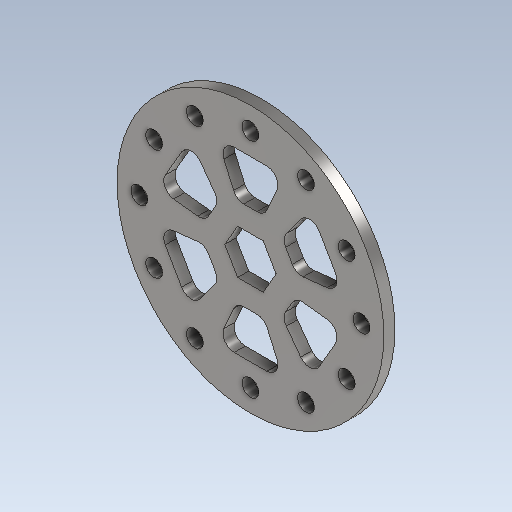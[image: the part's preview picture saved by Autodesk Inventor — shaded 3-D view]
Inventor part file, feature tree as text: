
AUTODESK INVENTOR PART (.ipt)
format: ipt  version: 2023 (Build 270158000, 158)  size: 222,208 bytes
history: native  units: in
note: dims shown in document units (in); Inventor stores cm internally (conversion verified against a paired STEP export)
features: extrude x2, sketch x1, fillet x1, pattern_circular x1
ambient origin geometry x8: Origin, YZ Plane, XZ Plane, XY Plane, X Axis, Y Axis, Z Axis, Center Point
bodies: Solid1 (feature_tree)
feature tree (5):
  sketch  "Sketch1"  dims[d0=3.0in d1=0.5in d2=2.5in d3=0.19in d4=4.7244in d6=360.0deg d8=0.125in d9=0.0in d10=0.125in d11=0.0in d12=0.125in d13=2.3622in d14=360.0deg d16=0.25in d18=0.3125in d19=0.75in d20=0.5in]
  extrude  "Extrusion1"  Depth=0.5in
  extrude  "Extrusion2"  Depth=0.5in
  fillet  "Fillet1"  Radius=0.19in
  pattern_circular  "Circular Pattern1"  Count=12 Angle=360.0deg
